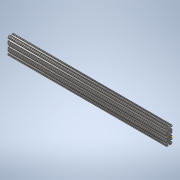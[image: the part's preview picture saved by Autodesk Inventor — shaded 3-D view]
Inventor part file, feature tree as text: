
AUTODESK INVENTOR PART (.ipt)
format: ipt  version: 2020 (Build 240168000, 168)  size: 390,144 bytes
history: native  units: in
note: dims shown in document units (in); Inventor stores cm internally (conversion verified against a paired STEP export)
features: sketch x2, extrude x1
ambient origin geometry x8: Origin, YZ Plane, XZ Plane, XY Plane, X Axis, Y Axis, Z Axis, Center Point
bodies: Solid1 (feature_tree)
feature tree (3):
  extrude  "Extrusion1"  [1 undecoded]
  sketch  "Sketch2"
  sketch  "Sketch1"  dims[d0=28.0in d1=0.0in]
note: 1 required parameter value undecoded (feature->parameter linkage not recoverable at this tier; creation-order binding heuristic only, values carry confidence <= 0.55)
